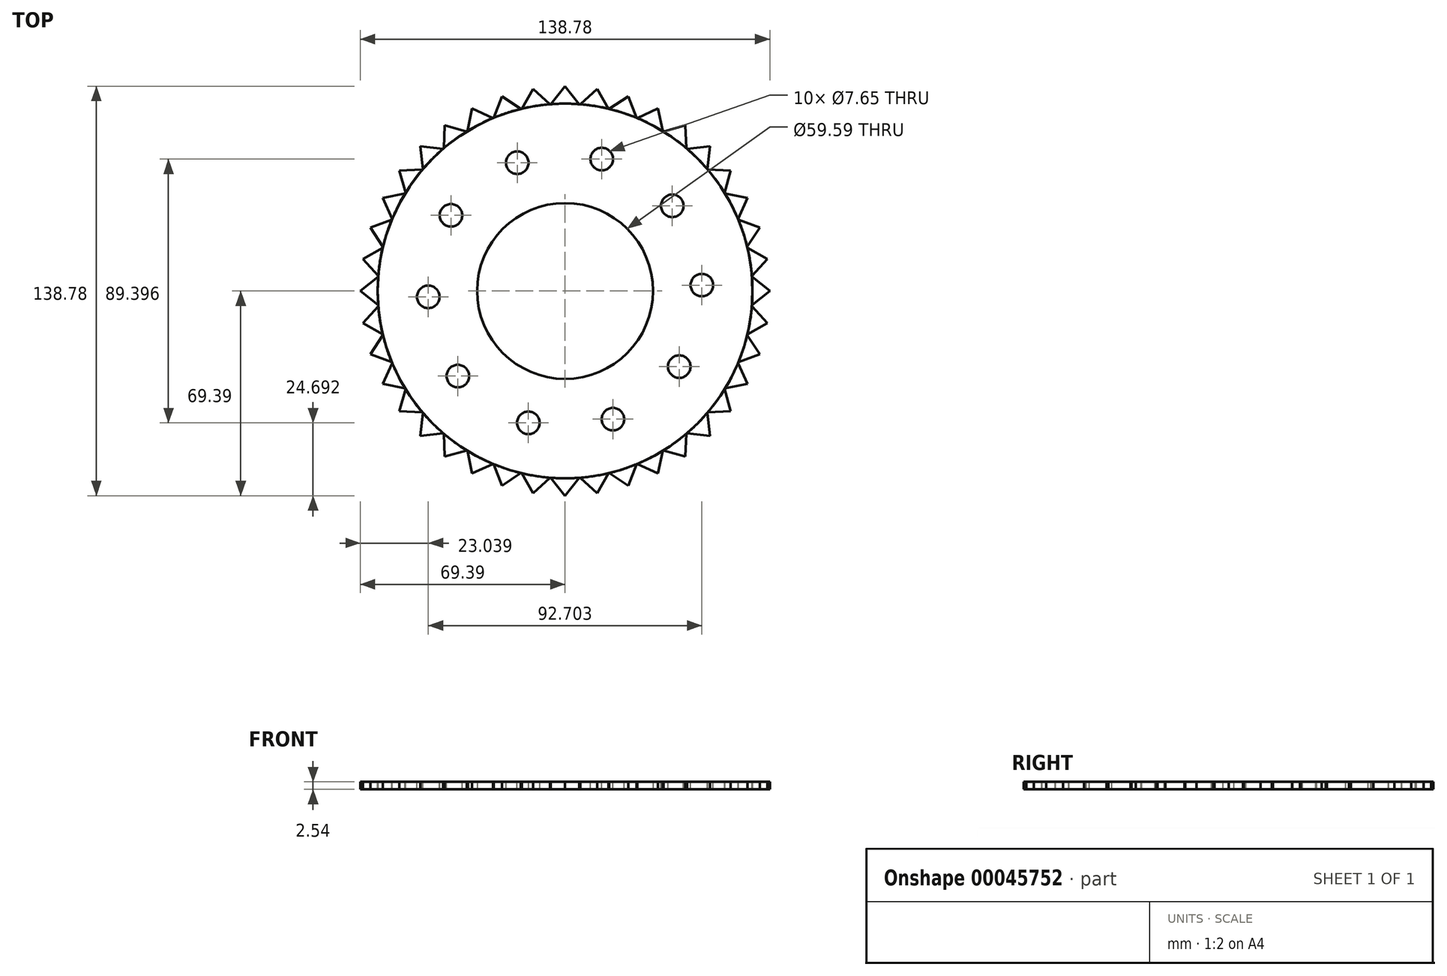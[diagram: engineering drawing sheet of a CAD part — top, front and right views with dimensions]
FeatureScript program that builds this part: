
annotation { "Feature Type Name" : "Feature", "Feature Type Description" : "" }
export const myFeature = defineFeature(function(context is Context, id is Id, definition is map)
    precondition{}
    {
        {
            var Q0;
            Q0=qCreatedBy(makeId("Top.planeOp"),FACE);
            var sketch = newSketch(context, id + "F0", { "sketchPlane" : qUnion([Q0])});
            skCircle(sketch, "E0", {"center": v(0, 0) * mm, "radius": 63.5 * mm});
            skSolve(sketch);
        }
        {
            var Q0;
            Q0=makeQuery(id+"F0.imprint","IMPRINT",FACE,{"disambiguationData":[TD([[makeQuery(id+"F0.imprint","IMPRINT",EDGE,{"derivedFrom":sQuery(id+"F0.wireOp",EDGE,"E0")}),1.0]])]});
            extrude(context, id + "F1", {"entities" : qUnion([Q0]), "endBound" : BoundingType.SYMMETRIC, "depth" : 2.54 * mm});
        }
        {
            var Q0;
            Q0=makeQuery(id+"F1.opExtrude","CAP_FACE",FACE,{"disambiguationData":[OSD([sQuery(id+"F0.wireOp",EDGE,"E0")])],"isStart":false});
            var sketch = newSketch(context, id + "F2", { "sketchPlane" : qUnion([Q0])});
            skCircle(sketch, "E1", {"center": v(-38.67, 25.63) * mm, "radius": 3.82 * mm});
            skSolve(sketch);
        }
        {
            var Q0;
            Q0=makeQuery(id+"F2.imprint","IMPRINT",FACE,{"disambiguationData":[TD([[makeQuery(id+"F2.imprint","IMPRINT",EDGE,{"derivedFrom":sQuery(id+"F2.wireOp",EDGE,"E1")}),1.0]])]});
            extrude(context, id + "F3", {"entities" : qUnion([Q0]), "oppositeDirection" : true, "depth" : 76.2 * mm});
        }
        {
            var Q0;
            Q0=makeQuery(id+"F3.opExtrude","SWEPT_BODY",BODY,{"disambiguationData":[OSD([sQuery(id+"F2.wireOp",EDGE,"E1")])]});
            var Q1;
            Q1=makeQuery(id+"F1.opExtrude","CAP_EDGE",EDGE,{"disambiguationData":[OSD([sQuery(id+"F0.wireOp",EDGE,"E0")])],"isStart":true});
            circularPattern(context, id + "F4", {"entities" : qUnion([Q0]), "axis" : qUnion([Q1]), "angle" : 360 * degree, "instanceCount" : 10, "equalSpace" : true});
        }
        {
            var Q0;
            Q0=makeQuery(id+"F3.opExtrude","SWEPT_BODY",BODY,{"disambiguationData":[OSD([sQuery(id+"F2.wireOp",EDGE,"E1")])]});
            var Q1;
            Q1=makeQuery(id+"F4.opPattern","COPY",BODY,{"derivedFrom":makeQuery(id+"F3.opExtrude","SWEPT_BODY",BODY,{"disambiguationData":[OSD([sQuery(id+"F2.wireOp",EDGE,"E1")])]}),"instanceName":"1"});
            var Q2;
            Q2=makeQuery(id+"F4.opPattern","COPY",BODY,{"derivedFrom":makeQuery(id+"F3.opExtrude","SWEPT_BODY",BODY,{"disambiguationData":[OSD([sQuery(id+"F2.wireOp",EDGE,"E1")])]}),"instanceName":"2"});
            var Q3;
            Q3=makeQuery(id+"F4.opPattern","COPY",BODY,{"derivedFrom":makeQuery(id+"F3.opExtrude","SWEPT_BODY",BODY,{"disambiguationData":[OSD([sQuery(id+"F2.wireOp",EDGE,"E1")])]}),"instanceName":"3"});
            var Q4;
            Q4=makeQuery(id+"F4.opPattern","COPY",BODY,{"derivedFrom":makeQuery(id+"F3.opExtrude","SWEPT_BODY",BODY,{"disambiguationData":[OSD([sQuery(id+"F2.wireOp",EDGE,"E1")])]}),"instanceName":"4"});
            var Q5;
            Q5=makeQuery(id+"F4.opPattern","COPY",BODY,{"derivedFrom":makeQuery(id+"F3.opExtrude","SWEPT_BODY",BODY,{"disambiguationData":[OSD([sQuery(id+"F2.wireOp",EDGE,"E1")])]}),"instanceName":"5"});
            var Q6;
            Q6=makeQuery(id+"F4.opPattern","COPY",BODY,{"derivedFrom":makeQuery(id+"F3.opExtrude","SWEPT_BODY",BODY,{"disambiguationData":[OSD([sQuery(id+"F2.wireOp",EDGE,"E1")])]}),"instanceName":"6"});
            var Q7;
            Q7=makeQuery(id+"F4.opPattern","COPY",BODY,{"derivedFrom":makeQuery(id+"F3.opExtrude","SWEPT_BODY",BODY,{"disambiguationData":[OSD([sQuery(id+"F2.wireOp",EDGE,"E1")])]}),"instanceName":"7"});
            var Q8;
            Q8=makeQuery(id+"F4.opPattern","COPY",BODY,{"derivedFrom":makeQuery(id+"F3.opExtrude","SWEPT_BODY",BODY,{"disambiguationData":[OSD([sQuery(id+"F2.wireOp",EDGE,"E1")])]}),"instanceName":"8"});
            var Q9;
            Q9=makeQuery(id+"F4.opPattern","COPY",BODY,{"derivedFrom":makeQuery(id+"F3.opExtrude","SWEPT_BODY",BODY,{"disambiguationData":[OSD([sQuery(id+"F2.wireOp",EDGE,"E1")])]}),"instanceName":"9"});
            var Q10;
            Q10=makeQuery(id+"F1.opExtrude","SWEPT_BODY",BODY,{"disambiguationData":[OSD([sQuery(id+"F0.wireOp",EDGE,"E0")])]});
            booleanBodies(context, id + "F5", {"operationType" : BooleanOperationType.SUBTRACTION, "tools" : qUnion([Q0, Q1, Q2, Q3, Q4, Q5, Q6, Q7, Q8, Q9]), "targets" : qUnion([Q10])});
        }
        {
            var Q0;
            Q0=makeQuery(id+"F1.opExtrude","CAP_FACE",FACE,{"disambiguationData":[OSD([sQuery(id+"F0.wireOp",EDGE,"E0")])],"isStart":false});
            var sketch = newSketch(context, id + "F6", { "sketchPlane" : qUnion([Q0])});
            skLineSegment(sketch, "E2", {"start": v(-4.83, 63.32) * mm, "end": v(0, 69.39) * mm});
            skLineSegment(sketch, "E3", {"start": v(0, 69.39) * mm, "end": v(4.83, 63.32) * mm});
            skArc(sketch, "E4.0", {"start": v(4.83, 63.32) * mm, "mid": v(0, 63.5) * mm, "end": v(-4.83, 63.32) * mm});
            skSolve(sketch);
        }
        {
            var Q0;
            Q0 = qSketchRegion(id + "F6", true);
            var Q1;
            Q1=makeQuery(id+"F1.opExtrude","CAP_FACE",FACE,{"disambiguationData":[OSD([sQuery(id+"F0.wireOp",EDGE,"E0")])],"isStart":true});
            extrude(context, id + "F7", {"entities" : qUnion([Q0]), "endBound" : BoundingType.UP_TO_SURFACE, "oppositeDirection" : true, "endBoundEntityFace" : qUnion([Q1]), "depth" : 25.4 * mm});
        }
        {
            var Q0;
            Q0=makeQuery(id+"F7.opExtrude","SWEPT_BODY",BODY,{"disambiguationData":[OSD([sQuery(id+"F6.wireOp",EDGE,"E2"),sQuery(id+"F6.wireOp",EDGE,"E3"),sQuery(id+"F6.wireOp",EDGE,"E4.0")])]});
            var Q1;
            Q1=makeQuery(id+"F1.opExtrude","CAP_EDGE",EDGE,{"disambiguationData":[OSD([sQuery(id+"F0.wireOp",EDGE,"E0")])],"isStart":false});
            circularPattern(context, id + "F8", {"entities" : qUnion([Q0]), "axis" : qUnion([Q1]), "angle" : 360 * degree, "instanceCount" : 40, "equalSpace" : true});
        }
        {
            var Q0;
            Q0=makeQuery(id+"F1.opExtrude","CAP_FACE",FACE,{"disambiguationData":[OSD([sQuery(id+"F0.wireOp",EDGE,"E0")])],"isStart":true});
            var sketch = newSketch(context, id + "F9", { "sketchPlane" : qUnion([Q0])});
            skCircle(sketch, "E5", {"center": v(0, 0) * mm, "radius": 29.8 * mm});
            skSolve(sketch);
        }
        {
            var Q0;
            Q0=makeQuery(id+"F9.imprint","IMPRINT",FACE,{"disambiguationData":[TD([[makeQuery(id+"F9.imprint","IMPRINT",EDGE,{"derivedFrom":sQuery(id+"F9.wireOp",EDGE,"E5")}),1.0]])]});
            var Q1;
            Q1=makeQuery(id+"F1.opExtrude","CAP_FACE",FACE,{"disambiguationData":[OSD([sQuery(id+"F0.wireOp",EDGE,"E0")])],"isStart":false});
            extrude(context, id + "F10", {"entities" : qUnion([Q0]), "operationType" : NewBodyOperationType.REMOVE, "endBound" : BoundingType.UP_TO_SURFACE, "oppositeDirection" : true, "endBoundEntityFace" : qUnion([Q1]), "depth" : 25.4 * mm});
        }
    });
